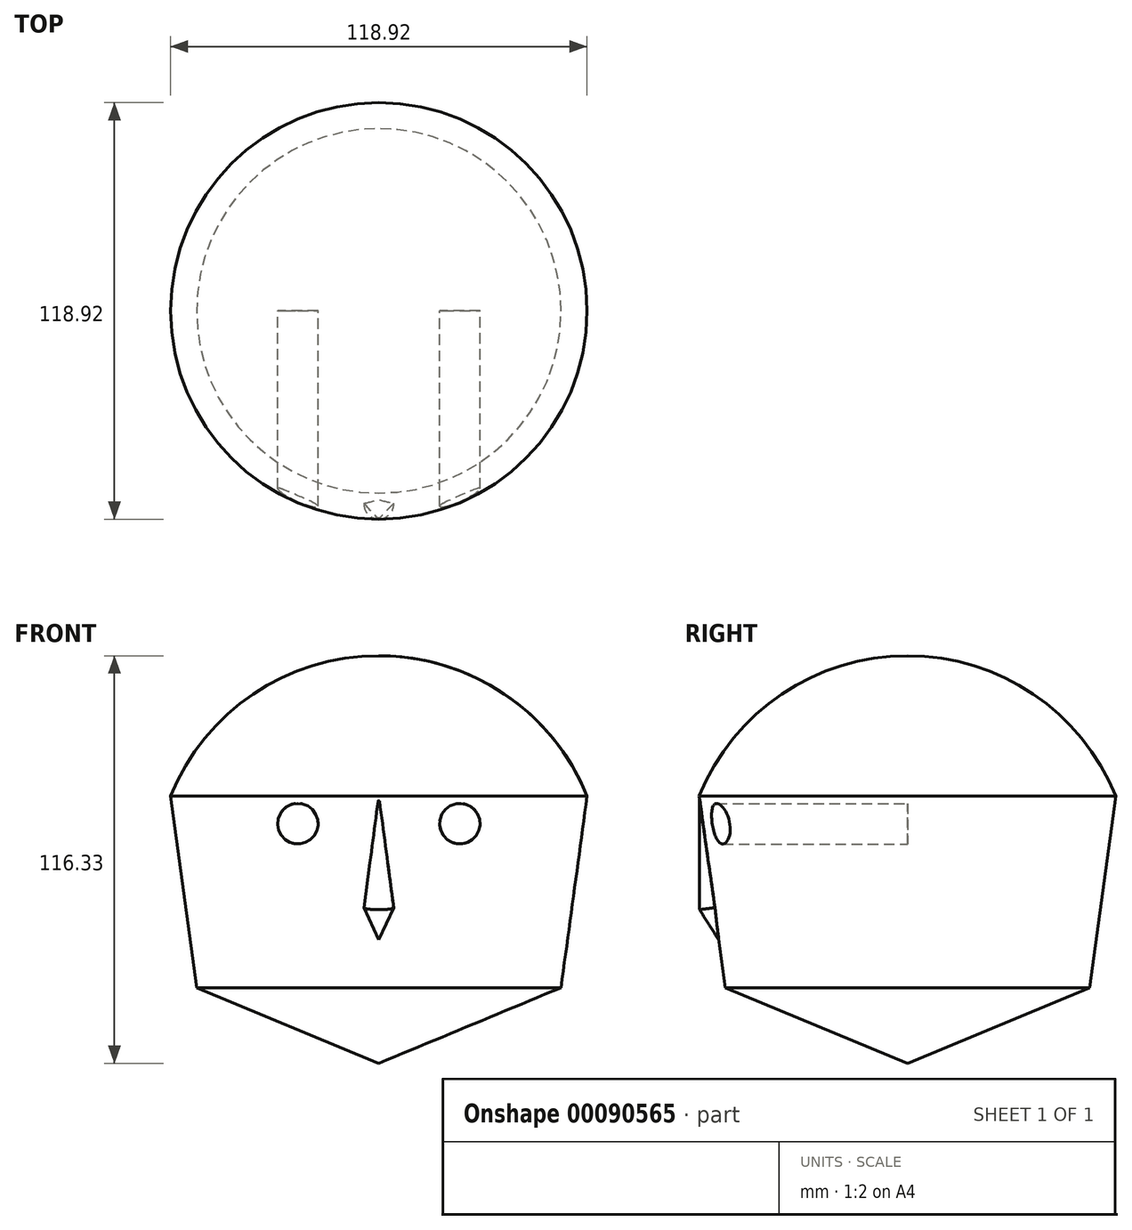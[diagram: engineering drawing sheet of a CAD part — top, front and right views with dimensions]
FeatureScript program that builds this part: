
annotation { "Feature Type Name" : "Feature", "Feature Type Description" : "" }
export const myFeature = defineFeature(function(context is Context, id is Id, definition is map)
    precondition{}
    {
        {
            var Q0;
            Q0=qCreatedBy(makeId("Front.planeOp"),FACE);
            var sketch = newSketch(context, id + "F0", { "sketchPlane" : qUnion([Q0])});
            skArc(sketch, "E0", {"start": v(0, 40.03) * mm, "mid": v(-35.84, 29.1) * mm, "end": v(-59.46, 0) * mm});
            skLineSegment(sketch, "E1", {"start": v(-59.46, 0) * mm, "end": v(-52, -54.71) * mm});
            skLineSegment(sketch, "E2", {"start": v(-52, -54.71) * mm, "end": v(0, -76.3) * mm});
            skLineSegment(sketch, "E3", {"start": v(0, 40.03) * mm, "end": v(0, -76.3) * mm});
            skPoint(sketch, "E4.orphan", {"position": v(0, 75.8) * mm});
            skPoint(sketch, "E5.MirrorCS.end.orphan", {"position": v(52, -54.71) * mm});
            skPoint(sketch, "E5.MirrorCS.start.orphan", {"position": v(59.46, 0) * mm});
            skPoint(sketch, "E6.MirrorCS.end.orphan", {"position": v(0, -76.3) * mm});
            skSolve(sketch);
        }
        {
            var Q0;
            Q0=qCreatedBy(makeId("Front.planeOp"),FACE);
            var sketch = newSketch(context, id + "F1", { "sketchPlane" : qUnion([Q0])});
            skLineSegment(sketch, "E7", {"start": v(0, 78.2) * mm, "end": v(0, -82.7) * mm});
            skSolve(sketch);
        }
        {
            var Q0;
            Q0 = qSketchRegion(id + "F0", true);
            var Q1;
            Q1=sQuery(id+"F1.wireOp",EDGE,"E7");
            revolve(context, id + "F2", {"entities" : qUnion([Q0]), "axis" : qUnion([Q1]), "revolveType" : RevolveType.FULL});
        }
        {
            var Q0;
            Q0=qCreatedBy(makeId("Right.planeOp"),FACE);
            var sketch = newSketch(context, id + "F3", { "sketchPlane" : qUnion([Q0])});
            skLineSegment(sketch, "E8", {"start": v(-59.37, 0) * mm, "end": v(-59.37, -32.45) * mm});
            skLineSegment(sketch, "E9", {"start": v(-59.37, -32.45) * mm, "end": v(-53.95, -41.01) * mm});
            skLineSegment(sketch, "E10", {"start": v(-59.37, 0) * mm, "end": v(-53.95, -41.01) * mm});
            skSolve(sketch);
        }
        {
            var Q0;
            Q0 = qSketchRegion(id + "F3", true);
            var Q1;
            Q1=sQuery(id+"F3.wireOp",EDGE,"E10");
            revolve(context, id + "F4", {"operationType" : NewBodyOperationType.ADD, "entities" : qUnion([Q0]), "axis" : qUnion([Q1]), "revolveType" : RevolveType.FULL});
        }
        {
            var Q0;
            Q0=qCreatedBy(makeId("Front.planeOp"),FACE);
            var sketch = newSketch(context, id + "F5", { "sketchPlane" : qUnion([Q0])});
            skCircle(sketch, "E11", {"center": v(-23.12, -7.9) * mm, "radius": 5.78 * mm});
            skCircle(sketch, "E12.MirrorC", {"center": v(23.12, -7.9) * mm, "radius": 5.78 * mm});
            skSolve(sketch);
        }
        {
            var Q0;
            Q0 = qSketchRegion(id + "F5", true);
            extrude(context, id + "F6", {"entities" : qUnion([Q0]), "operationType" : NewBodyOperationType.REMOVE, "endBound" : BoundingType.THROUGH_ALL, "depth" : 122.3 * mm});
        }
    });
